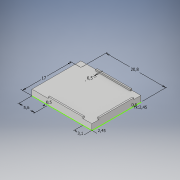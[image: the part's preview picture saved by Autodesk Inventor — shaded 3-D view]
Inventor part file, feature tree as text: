
AUTODESK INVENTOR PART (.ipt)
format: ipt  version: 2019 (Build 230136000, 136)  size: 125,952 bytes
history: native  units: mm
features: extrude x4, sketch x1
ambient origin geometry x8: Origin, YZ Plane, XZ Plane, XY Plane, X Axis, Y Axis, Z Axis, Center Point
bodies: Solid1 (feature_tree)
feature tree (5):
  sketch  "Sketch1"  dims[d0=20.8mm d1=17.0mm d2=0.5mm d3=2.45mm d4=2.45mm d5=3.1mm d6=5.6mm d7=0.5mm d8=0.5mm d9=2.0mm d10=0.0mm d11=2.5mm d12=0.0mm d13=2.5mm d14=0.0mm d15=2.5mm d16=0.0mm]
  extrude  "Extrusion1"  Depth=17.0mm
  extrude  "Extrusion2"  Depth=0.5mm
  extrude  "Extrusion3"  Depth=2.45mm
  extrude  "Extrusion4"  Depth=2.45mm
